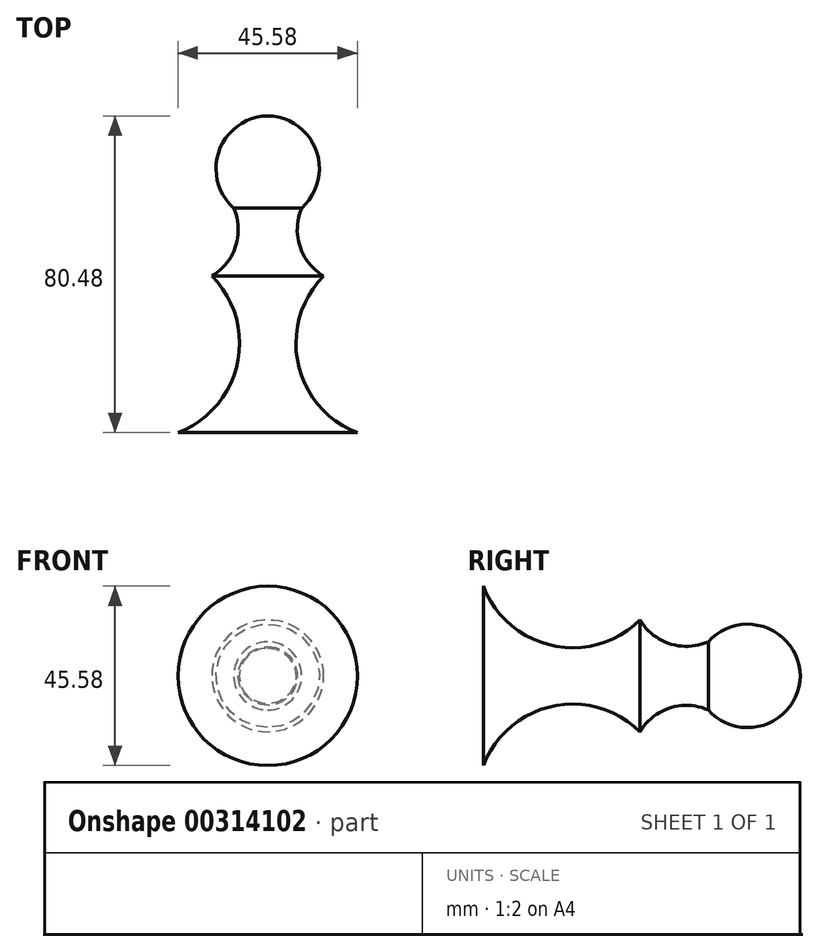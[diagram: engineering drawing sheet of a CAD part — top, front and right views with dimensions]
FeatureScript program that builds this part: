
annotation { "Feature Type Name" : "Feature", "Feature Type Description" : "" }
export const myFeature = defineFeature(function(context is Context, id is Id, definition is map)
    precondition{}
    {
        {
            var Q0;
            Q0=qCreatedBy(makeId("Top.planeOp"),FACE);
            var sketch = newSketch(context, id + "F0", { "sketchPlane" : qUnion([Q0])});
            skArc(sketch, "E0", {"start": v(0, 28.84) * mm, "mid": v(13.14, 42.21) * mm, "end": v(0, 55.59) * mm});
            skArc(sketch, "E1", {"start": v(8.65, 32.22) * mm, "mid": v(8.15, 22.5) * mm, "end": v(14.19, 14.89) * mm});
            skArc(sketch, "E2", {"start": v(14.19, 14.89) * mm, "mid": v(7.7, -7.33) * mm, "end": v(22.8, -24.89) * mm});
            skLineSegment(sketch, "E3", {"start": v(22.8, -24.89) * mm, "end": v(0, -24.89) * mm});
            skLineSegment(sketch, "E4", {"start": v(0, 55.59) * mm, "end": v(0, -24.89) * mm});
            skSolve(sketch);
        }
        {
            var Q0;
            {var subQ0=sQuery(id+"F0.wireOp",EDGE,"E4");var subQ1=sQuery(id+"F0.wireOp",EDGE,"E0");var subQ2=makeQuery(id+"F0.imprint","INTERSECT",VERTEX,{"disambiguationData":[OD(0.0)],"derivedFrom":[subQ1,subQ0]});Q0=makeQuery(id+"F0.imprint","IMPRINT",FACE,{"disambiguationData":[TD([[makeQuery(id+"F0.imprint","IMPRINT",EDGE,{"disambiguationData":[TD([[subQ2,-1.0]])],"derivedFrom":subQ1}),1.0]])]});}
            var Q1;
            {var subQ1=sQuery(id+"F0.wireOp",EDGE,"E1");Q1=makeQuery(id+"F0.imprint","IMPRINT",FACE,{"disambiguationData":[TD([[makeQuery(id+"F0.imprint","IMPRINT",EDGE,{"derivedFrom":subQ1}),-1.0]])]});}
            var Q2;
            Q2=sQuery(id+"F0.wireOp",EDGE,"E4");
            revolve(context, id + "F1", {"entities" : qUnion([Q0, Q1]), "axis" : qUnion([Q2]), "revolveType" : RevolveType.FULL});
        }
    });
